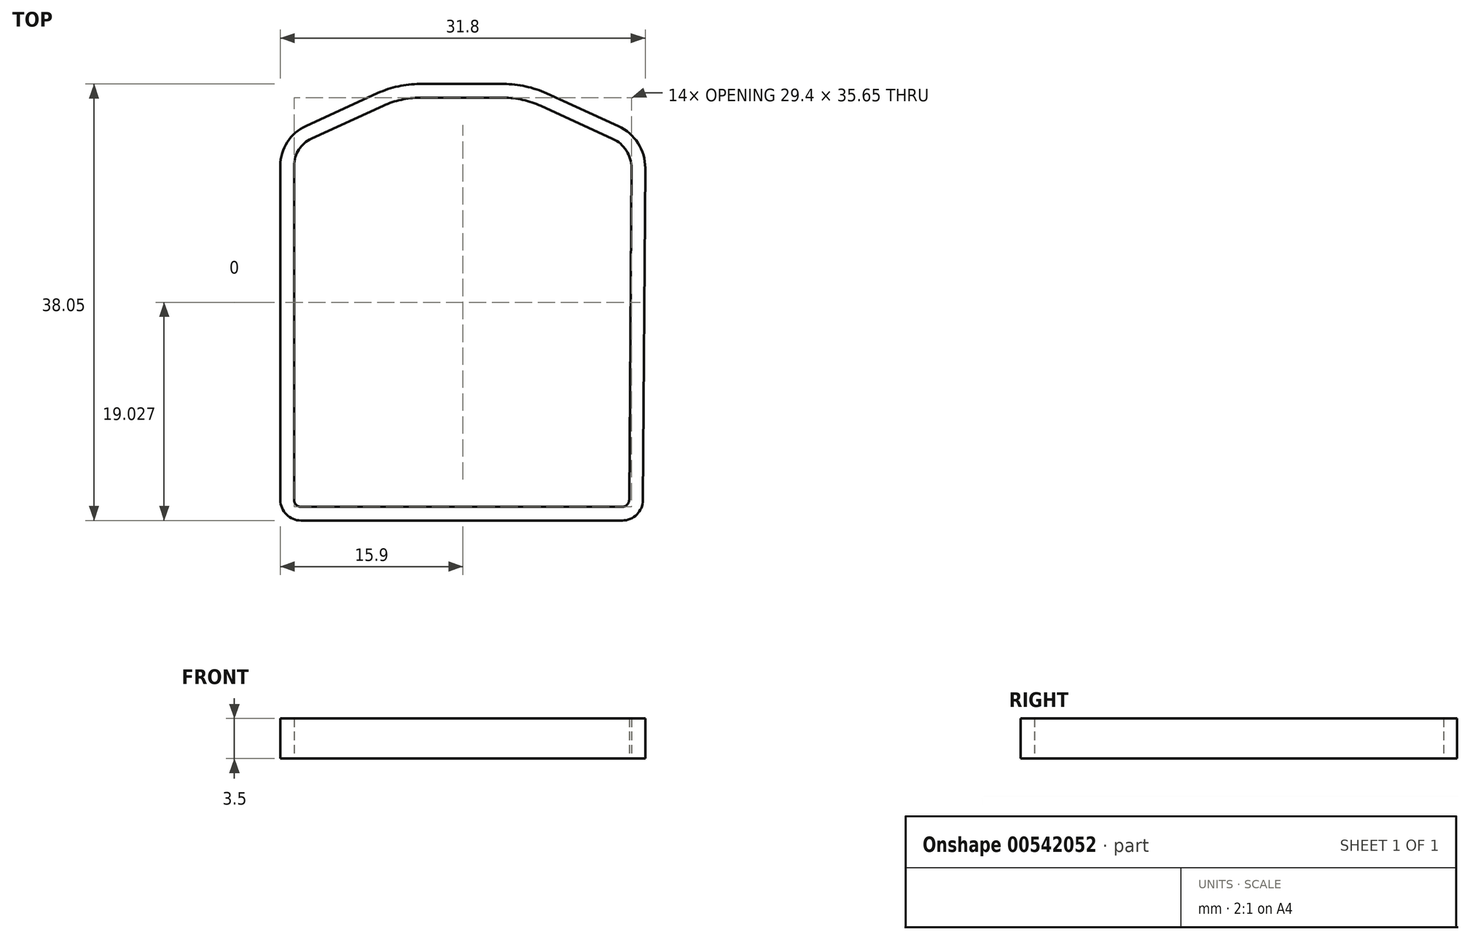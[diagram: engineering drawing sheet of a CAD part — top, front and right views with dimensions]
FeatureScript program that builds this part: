
annotation { "Feature Type Name" : "Feature", "Feature Type Description" : "" }
export const myFeature = defineFeature(function(context is Context, id is Id, definition is map)
    precondition{}
    {
        {
            var Q0;
            Q0=qCreatedBy(makeId("Top.planeOp"),FACE);
            var sketch = newSketch(context, id + "F0", { "sketchPlane" : qUnion([Q0])});
            skArc(sketch, "E0.0", {"start": v(-13.58, 17.59) * mm, "mid": v(-15.2, 16.19) * mm, "end": v(-15.8, 14.13) * mm});
            skLineSegment(sketch, "E0.1", {"start": v(16, 13.93) * mm, "end": v(15.8, -15.02) * mm});
            skArc(sketch, "E0.2", {"start": v(14, -16.8) * mm, "mid": v(15.27, -16.28) * mm, "end": v(15.8, -15.02) * mm});
            skLineSegment(sketch, "E0.3", {"start": v(-14, -16.8) * mm, "end": v(14, -16.8) * mm});
            skArc(sketch, "E0.4", {"start": v(-15.8, -15) * mm, "mid": v(-15.27, -16.27) * mm, "end": v(-14, -16.8) * mm});
            skArc(sketch, "E0.5", {"start": v(16, 13.93) * mm, "mid": v(15.37, 16.1) * mm, "end": v(13.66, 17.57) * mm});
            skLineSegment(sketch, "E0.6", {"start": v(-15.8, 14.13) * mm, "end": v(-15.8, -15) * mm});
            skLineSegment(sketch, "E0.7", {"start": v(13.66, 17.57) * mm, "end": v(7.4, 20.44) * mm});
            skArc(sketch, "E0.8", {"start": v(7.4, 20.44) * mm, "mid": v(5.57, 21.05) * mm, "end": v(3.66, 21.25) * mm});
            skLineSegment(sketch, "E0.9", {"start": v(-3.66, 21.25) * mm, "end": v(3.66, 21.25) * mm});
            skArc(sketch, "E0.10", {"start": v(-3.66, 21.25) * mm, "mid": v(-5.53, 21.05) * mm, "end": v(-7.32, 20.46) * mm});
            skLineSegment(sketch, "E0.11", {"start": v(-13.58, 17.59) * mm, "end": v(-7.32, 20.46) * mm});
            skArc(sketch, "E1.0", {"start": v(-13.08, 16.5) * mm, "mid": v(-14.19, 15.54) * mm, "end": v(-14.6, 14.13) * mm});
            skLineSegment(sketch, "E1.1", {"start": v(14.8, 13.93) * mm, "end": v(14.6, -15) * mm});
            skArc(sketch, "E1.2", {"start": v(14, -15.6) * mm, "mid": v(14.42, -15.42) * mm, "end": v(14.6, -15) * mm});
            skLineSegment(sketch, "E1.3", {"start": v(-14, -15.6) * mm, "end": v(14, -15.6) * mm});
            skArc(sketch, "E1.4", {"start": v(-14.6, -15) * mm, "mid": v(-14.42, -15.42) * mm, "end": v(-14, -15.6) * mm});
            skArc(sketch, "E1.5", {"start": v(14.8, 13.93) * mm, "mid": v(14.36, 15.45) * mm, "end": v(13.17, 16.48) * mm});
            skLineSegment(sketch, "E1.6", {"start": v(-14.6, 14.13) * mm, "end": v(-14.6, -15) * mm});
            skLineSegment(sketch, "E1.7", {"start": v(13.17, 16.48) * mm, "end": v(6.9, 19.35) * mm});
            skArc(sketch, "E1.8", {"start": v(6.9, 19.35) * mm, "mid": v(5.32, 19.87) * mm, "end": v(3.66, 20.05) * mm});
            skLineSegment(sketch, "E1.9", {"start": v(-3.66, 20.05) * mm, "end": v(3.66, 20.05) * mm});
            skArc(sketch, "E1.10", {"start": v(-3.66, 20.05) * mm, "mid": v(-5.28, 19.88) * mm, "end": v(-6.82, 19.36) * mm});
            skLineSegment(sketch, "E1.11", {"start": v(-13.08, 16.5) * mm, "end": v(-6.82, 19.36) * mm});
            skSolve(sketch);
        }
        {
            var Q0;
            Q0 = qSketchRegion(id + "F0", true);
            extrude(context, id + "F1", {"entities" : qUnion([Q0]), "depth" : 3.5 * mm, "offsetDistance" : 25 * mm});
        }
    });
